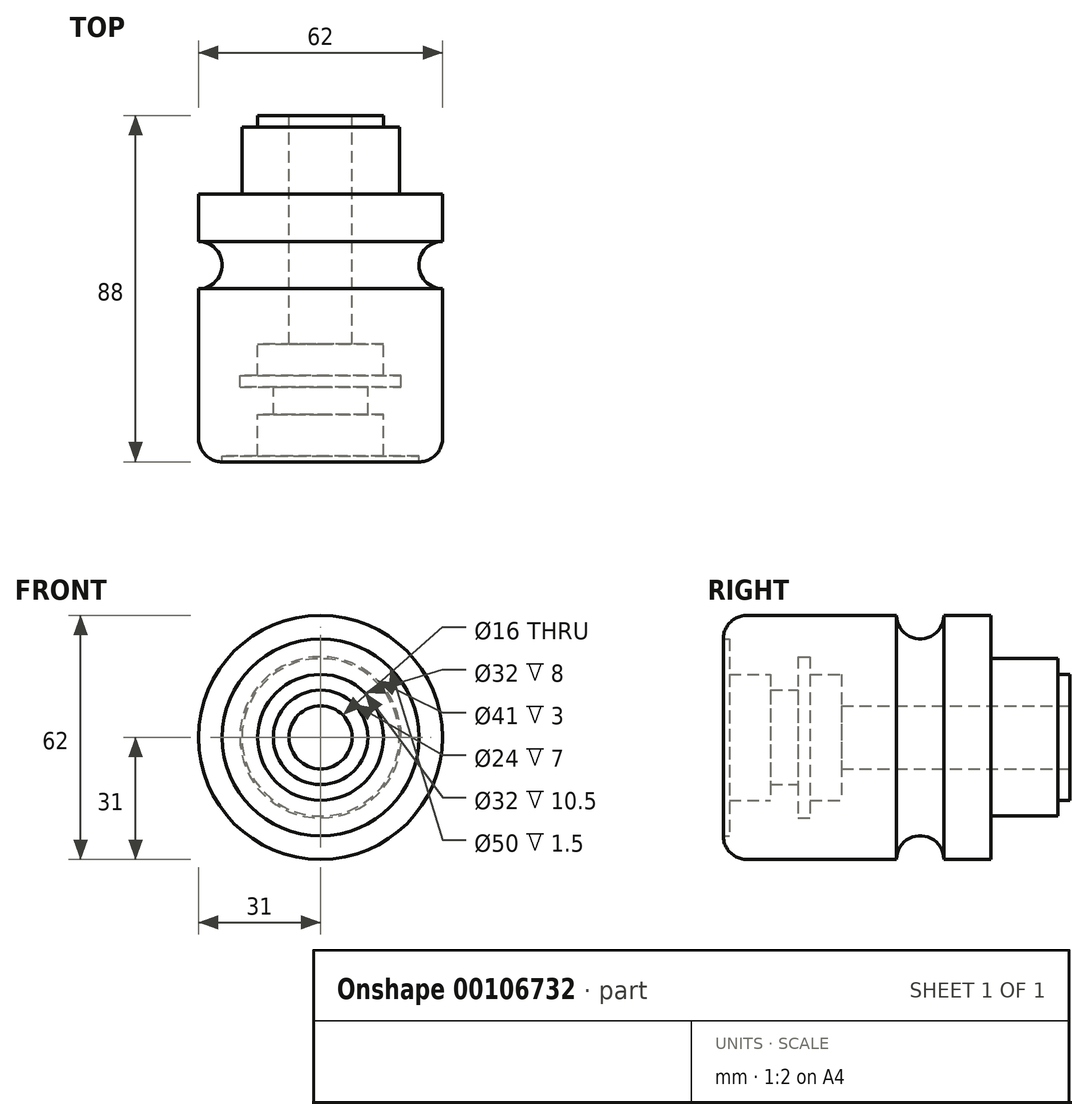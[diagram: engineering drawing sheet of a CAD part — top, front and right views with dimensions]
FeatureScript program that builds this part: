
annotation { "Feature Type Name" : "Feature", "Feature Type Description" : "" }
export const myFeature = defineFeature(function(context is Context, id is Id, definition is map)
    precondition{}
    {
        {
            var Q0;
            Q0=qCreatedBy(makeId("Right.planeOp"),FACE);
            var sketch = newSketch(context, id + "F0", { "sketchPlane" : qUnion([Q0])});
            skLineSegment(sketch, "E0.bottom", {"start": v(0, 0) * mm, "end": v(-44, 0) * mm});
            skLineSegment(sketch, "E0.top", {"start": v(0, 31) * mm, "end": v(-38, 31) * mm});
            skLineSegment(sketch, "E0.left", {"start": v(0, 0) * mm, "end": v(0, 31) * mm});
            skLineSegment(sketch, "E0.right", {"start": v(-44, 0) * mm, "end": v(-44, 25) * mm});
            skLineSegment(sketch, "E1.bottom", {"start": v(0, 0) * mm, "end": v(12, 0) * mm});
            skLineSegment(sketch, "E1.right", {"start": v(12, 0) * mm, "end": v(12, 31) * mm});
            skLineSegment(sketch, "E2.bottom", {"start": v(12, 31) * mm, "end": v(24, 31) * mm});
            skLineSegment(sketch, "E2.top", {"start": v(12, 0) * mm, "end": v(24, 0) * mm});
            skLineSegment(sketch, "E2.left", {"start": v(12, 31) * mm, "end": v(12, 0) * mm});
            skLineSegment(sketch, "E2.right", {"start": v(24, 31) * mm, "end": v(24, 0) * mm});
            skLineSegment(sketch, "E3.bottom", {"start": v(24, 0) * mm, "end": v(41, 0) * mm});
            skLineSegment(sketch, "E3.top", {"start": v(24, 20) * mm, "end": v(41, 20) * mm});
            skLineSegment(sketch, "E3.left", {"start": v(24, 0) * mm, "end": v(24, 20) * mm});
            skLineSegment(sketch, "E3.right", {"start": v(41, 0) * mm, "end": v(41, 20) * mm});
            skLineSegment(sketch, "E4.bottom", {"start": v(41, 16) * mm, "end": v(44, 16) * mm});
            skLineSegment(sketch, "E4.top", {"start": v(41, 0) * mm, "end": v(44, 0) * mm});
            skLineSegment(sketch, "E4.left", {"start": v(41, 16) * mm, "end": v(41, 0) * mm});
            skLineSegment(sketch, "E4.right", {"start": v(44, 16) * mm, "end": v(44, 0) * mm});
            skPoint(sketch, "E5.visualSharp", {"position": v(-44, 31) * mm});
            skArc(sketch, "E5.filletArc", {"start": v(-38, 31) * mm, "mid": v(-42.24, 29.24) * mm, "end": v(-44, 25) * mm});
            skArc(sketch, "E6", {"start": v(0, 31) * mm, "mid": v(6, 25) * mm, "end": v(12, 31) * mm});
            skSolve(sketch);
        }
        {
            var Q0;
            Q0 = qSketchRegion(id + "F0", true);
            var Q1;
            Q1=sQuery(id+"F0.wireOp",EDGE,"E1.bottom");
            revolve(context, id + "F1", {"entities" : qUnion([Q0]), "axis" : qUnion([Q1]), "revolveType" : RevolveType.FULL});
        }
        {
            var Q0;
            Q0=qCreatedBy(makeId("Right.planeOp"),FACE);
            var sketch = newSketch(context, id + "F2", { "sketchPlane" : qUnion([Q0])});
            skLineSegment(sketch, "E7.bottom", {"start": v(-44, 25) * mm, "end": v(-42.5, 25) * mm});
            skLineSegment(sketch, "E7.top", {"start": v(-44, 0) * mm, "end": v(-42.5, 0) * mm});
            skLineSegment(sketch, "E7.left", {"start": v(-44, 25) * mm, "end": v(-44, 0) * mm});
            skLineSegment(sketch, "E7.right", {"start": v(-42.5, 25) * mm, "end": v(-42.5, 0) * mm});
            skLineSegment(sketch, "E8.bottom", {"start": v(-42.5, 0) * mm, "end": v(-32, 0) * mm});
            skLineSegment(sketch, "E8.top", {"start": v(-42.5, 16) * mm, "end": v(-32, 16) * mm});
            skLineSegment(sketch, "E8.left", {"start": v(-42.5, 0) * mm, "end": v(-42.5, 16) * mm});
            skLineSegment(sketch, "E8.right", {"start": v(-32, 0) * mm, "end": v(-32, 16) * mm});
            skLineSegment(sketch, "E9.bottom", {"start": v(-32, 12) * mm, "end": v(-25, 12) * mm});
            skLineSegment(sketch, "E9.top", {"start": v(-32, 0) * mm, "end": v(-25, 0) * mm});
            skLineSegment(sketch, "E9.left", {"start": v(-32, 12) * mm, "end": v(-32, 0) * mm});
            skLineSegment(sketch, "E9.right", {"start": v(-25, 12) * mm, "end": v(-25, 0) * mm});
            skLineSegment(sketch, "E10.bottom", {"start": v(-25, 0) * mm, "end": v(-22, 0) * mm});
            skLineSegment(sketch, "E10.top", {"start": v(-25, 20.5) * mm, "end": v(-22, 20.5) * mm});
            skLineSegment(sketch, "E10.left", {"start": v(-25, 0) * mm, "end": v(-25, 20.5) * mm});
            skLineSegment(sketch, "E10.right", {"start": v(-22, 0) * mm, "end": v(-22, 20.5) * mm});
            skLineSegment(sketch, "E11.bottom", {"start": v(-22, 16) * mm, "end": v(-14, 16) * mm});
            skLineSegment(sketch, "E11.top", {"start": v(-22, 0) * mm, "end": v(-14, 0) * mm});
            skLineSegment(sketch, "E11.left", {"start": v(-22, 16) * mm, "end": v(-22, 0) * mm});
            skLineSegment(sketch, "E11.right", {"start": v(-14, 16) * mm, "end": v(-14, 0) * mm});
            skLineSegment(sketch, "E12.bottom", {"start": v(-14, 0) * mm, "end": v(44, 0) * mm});
            skLineSegment(sketch, "E12.top", {"start": v(-14, 8) * mm, "end": v(44, 8) * mm});
            skLineSegment(sketch, "E12.left", {"start": v(-14, 0) * mm, "end": v(-14, 8) * mm});
            skLineSegment(sketch, "E12.right", {"start": v(44, 0) * mm, "end": v(44, 8) * mm});
            skSolve(sketch);
        }
        {
            var Q0;
            Q0 = qSketchRegion(id + "F2", true);
            var Q1;
            Q1=sQuery(id+"F2.wireOp",EDGE,"E12.bottom");
            revolve(context, id + "F3", {"operationType" : NewBodyOperationType.REMOVE, "entities" : qUnion([Q0]), "axis" : qUnion([Q1]), "revolveType" : RevolveType.FULL, "oppositeDirection" : true});
        }
    });
